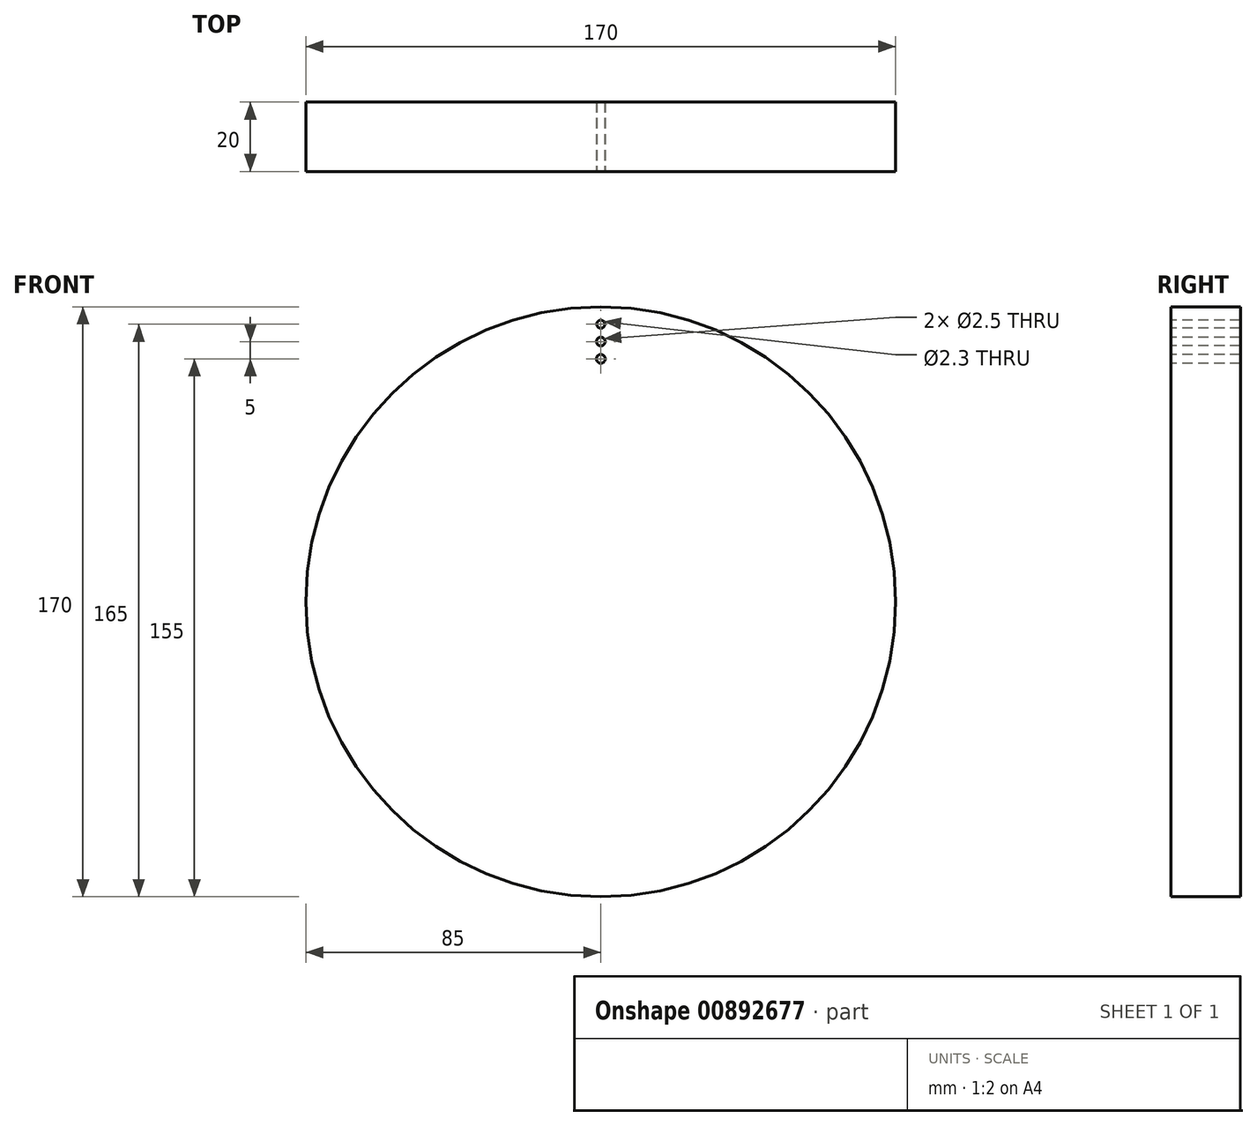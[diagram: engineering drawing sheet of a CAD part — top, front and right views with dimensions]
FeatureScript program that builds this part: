
annotation { "Feature Type Name" : "Feature", "Feature Type Description" : "" }
export const myFeature = defineFeature(function(context is Context, id is Id, definition is map)
    precondition{}
    {
        {
            var Q0;
            Q0=qCreatedBy(makeId("Front.planeOp"),FACE);
            var sketch = newSketch(context, id + "F0", { "sketchPlane" : qUnion([Q0])});
            skCircle(sketch, "E0", {"center": v(0, 0) * mm, "radius": 85 * mm});
            skSolve(sketch);
        }
        {
            var Q0;
            Q0 = qSketchRegion(id + "F0", true);
            var Q1;
            Q1=sQuery(id+"F0.wireOp",EDGE,"E0");
            extrude(context, id + "F1", {"entities" : qUnion([Q0]), "surfaceEntities" : qUnion([Q1]), "depth" : 20 * mm, "offsetDistance" : 25 * mm});
        }
        {
            var Q0;
            Q0=makeQuery(id+"F1.opExtrude","CAP_FACE",FACE,{"disambiguationData":[OSD([sQuery(id+"F0.wireOp",EDGE,"E0")])],"isStart":false});
            var sketch = newSketch(context, id + "F2", { "sketchPlane" : qUnion([Q0])});
            skCircle(sketch, "E1", {"center": v(0, 75) * mm, "radius": 1.25 * mm});
            skCircle(sketch, "E2", {"center": v(0, 70) * mm, "radius": 1.25 * mm});
            skCircle(sketch, "E3", {"center": v(0, 80) * mm, "radius": 1.15 * mm});
            skSolve(sketch);
        }
        {
            var Q0;
            Q0 = qSketchRegion(id + "F2", true);
            extrude(context, id + "F3", {"entities" : qUnion([Q0]), "operationType" : NewBodyOperationType.REMOVE, "oppositeDirection" : true, "depth" : 25 * mm, "offsetDistance" : 25 * mm});
        }
    });
